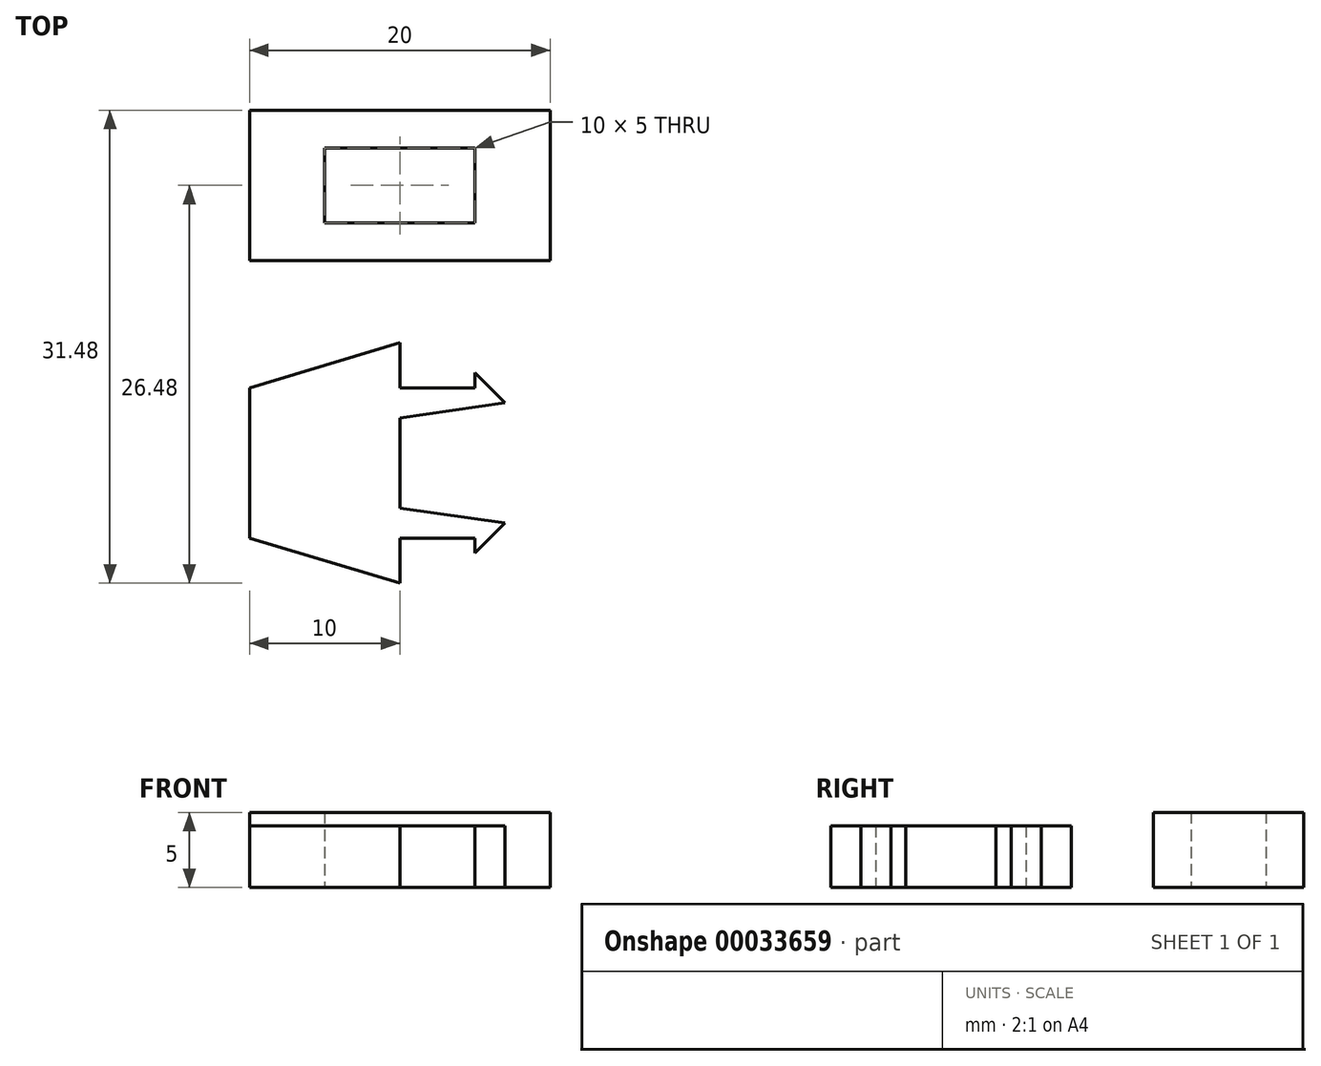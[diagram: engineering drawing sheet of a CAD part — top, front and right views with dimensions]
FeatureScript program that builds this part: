
annotation { "Feature Type Name" : "Feature", "Feature Type Description" : "" }
export const myFeature = defineFeature(function(context is Context, id is Id, definition is map)
    precondition{}
    {
        {
            var Q0;
            Q0=qCreatedBy(makeId("Top.planeOp"),FACE);
            var sketch = newSketch(context, id + "F0", { "sketchPlane" : qUnion([Q0])});
            skLineSegment(sketch, "E0.bottom", {"start": v(0, 0) * mm, "end": v(20, 0) * mm});
            skLineSegment(sketch, "E0.top", {"start": v(0, 10) * mm, "end": v(20, 10) * mm});
            skLineSegment(sketch, "E0.left", {"start": v(0, 0) * mm, "end": v(0, 10) * mm});
            skLineSegment(sketch, "E0.right", {"start": v(20, 0) * mm, "end": v(20, 10) * mm});
            skSolve(sketch);
        }
        {
            var Q0;
            Q0=makeQuery(id+"F0.imprint","IMPRINT",FACE,{"disambiguationData":[TD([[makeQuery(id+"F0.imprint","IMPRINT",EDGE,{"derivedFrom":sQuery(id+"F0.wireOp",EDGE,"E0.bottom")}),1.0]])]});
            var sketch = newSketch(context, id + "F1", { "sketchPlane" : qUnion([Q0])});
            skLineSegment(sketch, "E1.bottom", {"start": v(5, 7.5) * mm, "end": v(15, 7.5) * mm});
            skLineSegment(sketch, "E1.top", {"start": v(5, 2.5) * mm, "end": v(15, 2.5) * mm});
            skLineSegment(sketch, "E1.left", {"start": v(5, 7.5) * mm, "end": v(5, 2.5) * mm});
            skLineSegment(sketch, "E1.right", {"start": v(15, 7.5) * mm, "end": v(15, 2.5) * mm});
            skSolve(sketch);
        }
        {
            var Q0;
            Q0 = qSketchRegion(id + "F0", true);
            extrude(context, id + "F2", {"entities" : qUnion([Q0]), "depth" : 5 * mm});
        }
        {
            var Q0;
            Q0 = qSketchRegion(id + "F1", true);
            extrude(context, id + "F3", {"entities" : qUnion([Q0]), "operationType" : NewBodyOperationType.REMOVE, "endBound" : BoundingType.THROUGH_ALL, "depth" : 25 * mm});
        }
        {
            var Q0;
            Q0=qCreatedBy(makeId("Top.planeOp"),FACE);
            var sketch = newSketch(context, id + "F4", { "sketchPlane" : qUnion([Q0])});
            skLineSegment(sketch, "E2", {"start": v(15, -8.48) * mm, "end": v(15, -7.48) * mm});
            skLineSegment(sketch, "E3", {"start": v(15, -7.48) * mm, "end": v(17, -9.48) * mm});
            skLineSegment(sketch, "E4", {"start": v(17, -9.48) * mm, "end": v(10, -10.48) * mm});
            skLineSegment(sketch, "E5", {"start": v(10, -10.48) * mm, "end": v(10, -16.48) * mm});
            skLineSegment(sketch, "E6", {"start": v(10, -16.48) * mm, "end": v(17, -17.48) * mm});
            skLineSegment(sketch, "E7", {"start": v(17, -17.48) * mm, "end": v(15, -19.48) * mm});
            skLineSegment(sketch, "E8", {"start": v(15, -19.48) * mm, "end": v(15, -18.48) * mm});
            skLineSegment(sketch, "E9", {"start": v(0, -18.48) * mm, "end": v(0, -8.48) * mm});
            skLineSegment(sketch, "E10", {"start": v(0, -8.48) * mm, "end": v(10, -5.48) * mm});
            skLineSegment(sketch, "E11", {"start": v(10, -5.48) * mm, "end": v(10, -8.48) * mm});
            skLineSegment(sketch, "E12", {"start": v(0, -18.48) * mm, "end": v(10, -21.48) * mm});
            skLineSegment(sketch, "E13", {"start": v(10, -21.48) * mm, "end": v(10, -18.48) * mm});
            skLineSegment(sketch, "E14", {"start": v(10, -8.48) * mm, "end": v(15, -8.48) * mm});
            skLineSegment(sketch, "E15", {"start": v(10, -18.48) * mm, "end": v(15, -18.48) * mm});
            skSolve(sketch);
        }
        {
            var Q0;
            Q0 = qSketchRegion(id + "F4", true);
            extrude(context, id + "F5", {"entities" : qUnion([Q0]), "depth" : 4.1 * mm});
        }
    });
